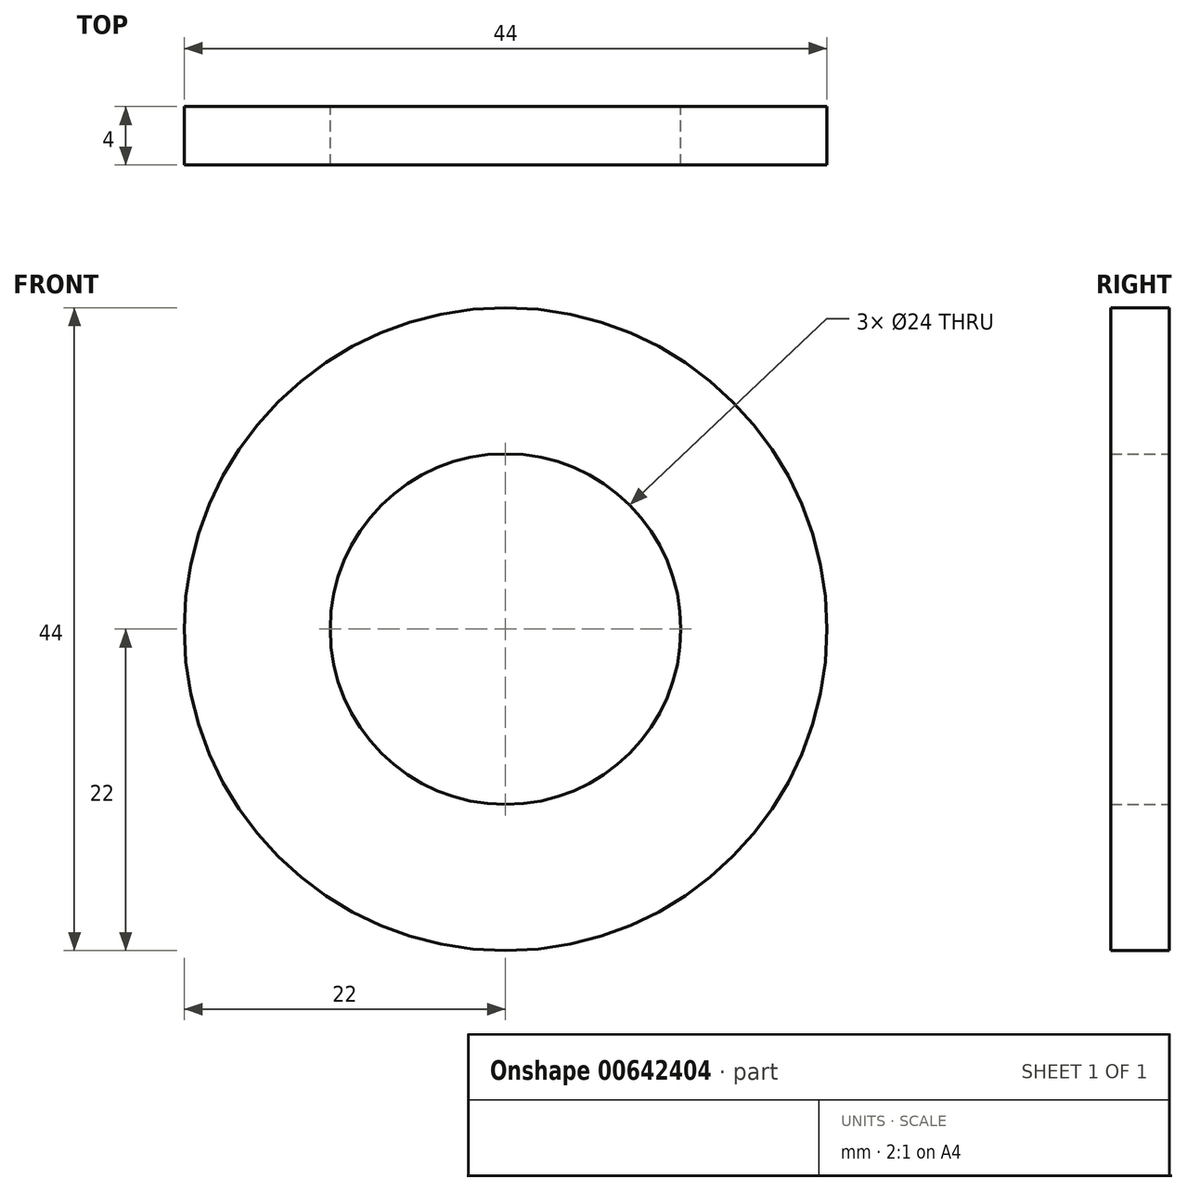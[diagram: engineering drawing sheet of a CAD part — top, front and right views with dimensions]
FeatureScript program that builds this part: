
annotation { "Feature Type Name" : "Feature", "Feature Type Description" : "" }
export const myFeature = defineFeature(function(context is Context, id is Id, definition is map)
    precondition{}
    {
        {
            var Q0;
            Q0=qCreatedBy(makeId("Front.planeOp"),FACE);
            var sketch = newSketch(context, id + "F0", { "sketchPlane" : qUnion([Q0])});
            skCircle(sketch, "E0", {"center": v(0, 0) * mm, "radius": 12 * mm});
            skCircle(sketch, "E1", {"center": v(0, 0) * mm, "radius": 22 * mm});
            skSolve(sketch);
        }
        {
            var Q0;
            Q0=makeQuery(id+"F0.imprint","IMPRINT",FACE,{"disambiguationData":[TD([[makeQuery(id+"F0.imprint","IMPRINT",EDGE,{"derivedFrom":sQuery(id+"F0.wireOp",EDGE,"E0")}),-1.0]])]});
            extrude(context, id + "F1", {"entities" : qUnion([Q0]), "depth" : 4 * mm, "offsetDistance" : 25 * mm});
        }
    });
